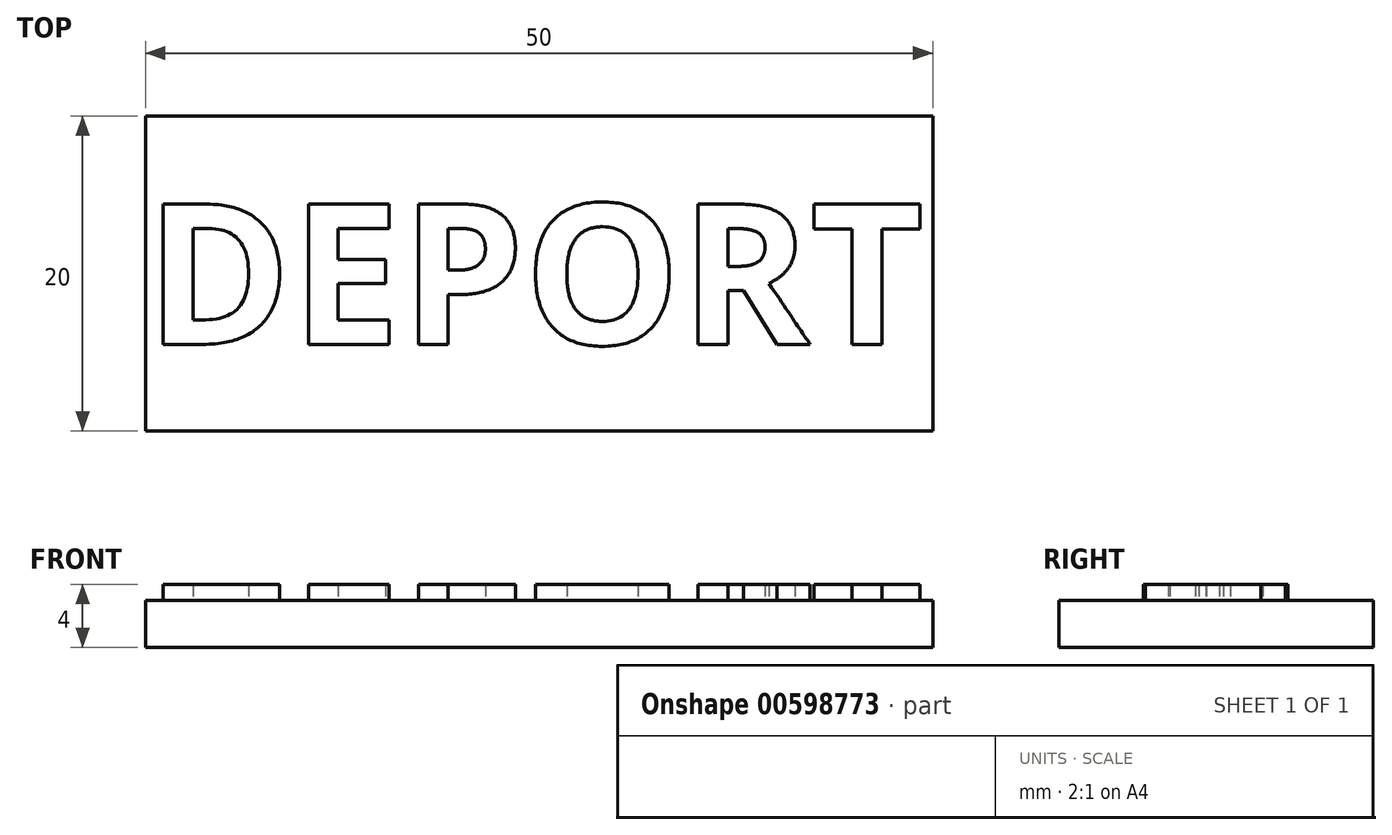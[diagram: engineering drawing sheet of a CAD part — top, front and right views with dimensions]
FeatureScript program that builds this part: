
annotation { "Feature Type Name" : "Feature", "Feature Type Description" : "" }
export const myFeature = defineFeature(function(context is Context, id is Id, definition is map)
    precondition{}
    {
        {
            var Q0;
            Q0=qCreatedBy(makeId("Top.planeOp"),FACE);
            var sketch = newSketch(context, id + "F0", { "sketchPlane" : qUnion([Q0])});
            skLineSegment(sketch, "E0.bottom", {"start": v(25, -10) * mm, "end": v(-25, -10) * mm});
            skLineSegment(sketch, "E0.top", {"start": v(25, 10) * mm, "end": v(-25, 10) * mm});
            skLineSegment(sketch, "E0.left", {"start": v(25, -10) * mm, "end": v(25, 10) * mm});
            skLineSegment(sketch, "E0.right", {"start": v(-25, -10) * mm, "end": v(-25, 10) * mm});
            skPoint(sketch, "E0.middle", {"position": v(0, 0) * mm});
            skSolve(sketch);
        }
        {
            var Q0;
            Q0=makeQuery(id+"F0.imprint","IMPRINT",FACE,{"disambiguationData":[TD([[makeQuery(id+"F0.imprint","IMPRINT",EDGE,{"derivedFrom":sQuery(id+"F0.wireOp",EDGE,"E0.bottom")}),-1.0]])]});
            extrude(context, id + "F1", {"entities" : qUnion([Q0]), "oppositeDirection" : true, "depth" : 3 * mm, "offsetDistance" : 25 * mm});
        }
        {
            var Q0;
            Q0=qCreatedBy(makeId("Top.planeOp"),FACE);
            var sketch = newSketch(context, id + "F2", { "sketchPlane" : qUnion([Q0])});
            skText(sketch, "E1", { "text": "DEPORT", "fontName": "OpenSans-Bold.ttf"});
            skPoint(sketch, "E2", {"position": v(0, 0) * mm});
            const initialGuessF2  = {"E1": [-0.025, -0.0045, 1, 0, 0.00898]};
            skSetInitialGuess(sketch, initialGuessF2);
            skSolve(sketch);
        }
        {
            var Q0;
            Q0 = qSketchRegion(id + "F2", true);
            extrude(context, id + "F3", {"entities" : qUnion([Q0]), "operationType" : NewBodyOperationType.ADD, "depth" : 1 * mm, "offsetDistance" : 25 * mm});
        }
    });
